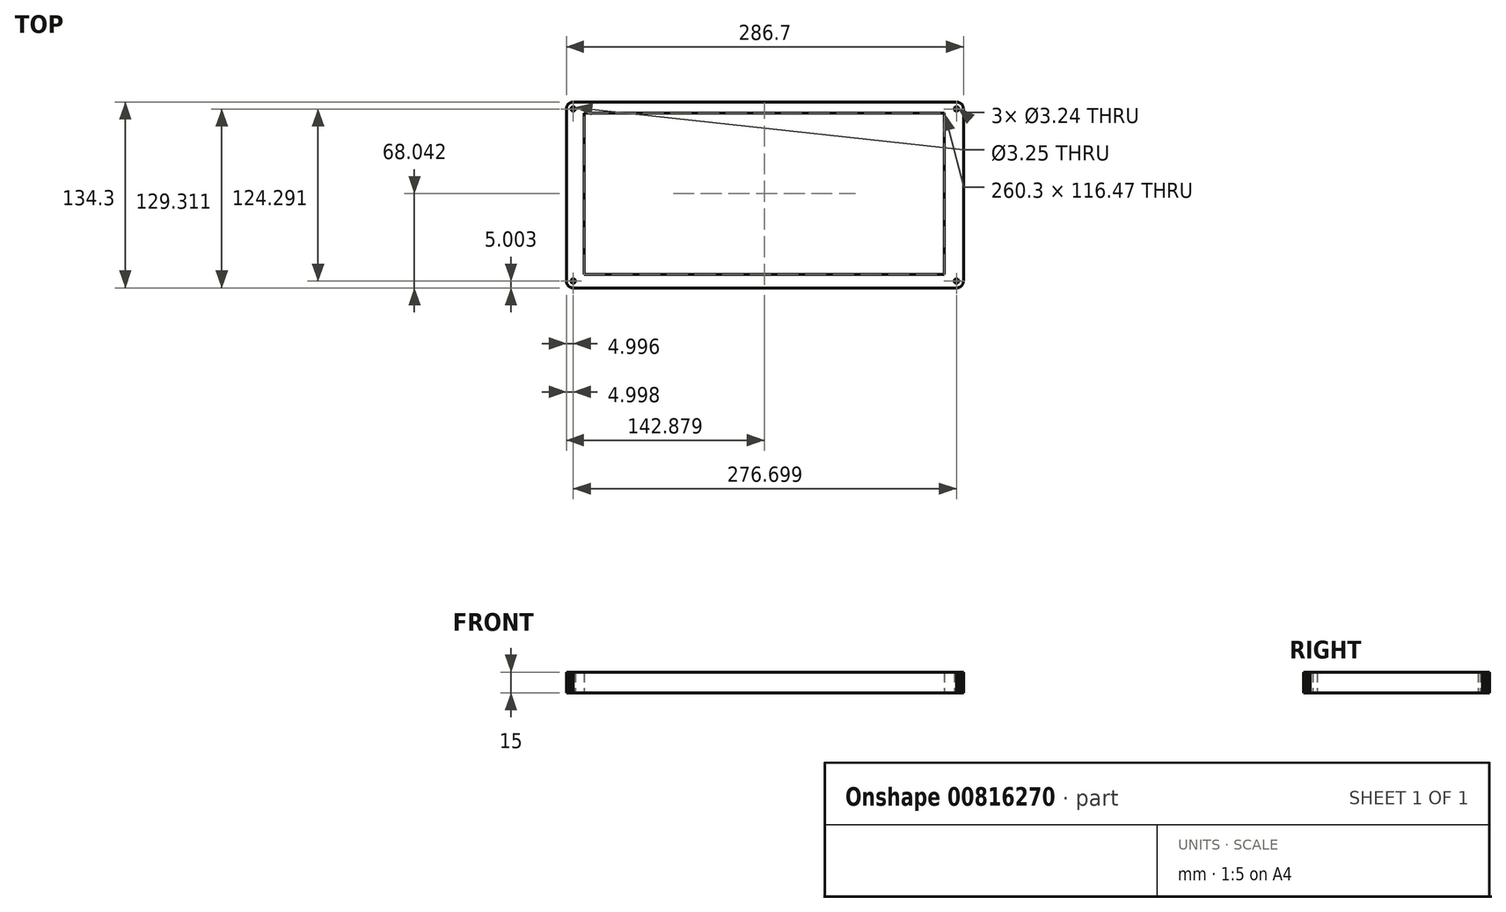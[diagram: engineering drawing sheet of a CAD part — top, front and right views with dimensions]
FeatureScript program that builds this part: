
annotation { "Feature Type Name" : "Feature", "Feature Type Description" : "" }
export const myFeature = defineFeature(function(context is Context, id is Id, definition is map)
    precondition{}
    {
        {
            var Q0;
            Q0=qCreatedBy(makeId("Top.planeOp"),FACE);
            var sketch = newSketch(context, id + "F0", { "sketchPlane" : qUnion([Q0])});
            skLineSegment(sketch, "E0", {"start": v(138.35, 67.15) * mm, "end": v(138.74, 67.13) * mm});
            skLineSegment(sketch, "E1", {"start": v(138.74, 67.13) * mm, "end": v(139.13, 67.09) * mm});
            skLineSegment(sketch, "E2", {"start": v(139.13, 67.09) * mm, "end": v(139.52, 67.01) * mm});
            skLineSegment(sketch, "E3", {"start": v(139.52, 67.01) * mm, "end": v(139.9, 66.9) * mm});
            skLineSegment(sketch, "E4", {"start": v(139.9, 66.9) * mm, "end": v(140.26, 66.77) * mm});
            skLineSegment(sketch, "E5", {"start": v(140.26, 66.77) * mm, "end": v(140.62, 66.6) * mm});
            skLineSegment(sketch, "E6", {"start": v(140.62, 66.6) * mm, "end": v(140.96, 66.41) * mm});
            skLineSegment(sketch, "E7", {"start": v(140.96, 66.41) * mm, "end": v(141.29, 66.2) * mm});
            skLineSegment(sketch, "E8", {"start": v(141.29, 66.2) * mm, "end": v(141.6, 65.95) * mm});
            skLineSegment(sketch, "E9", {"start": v(141.6, 65.95) * mm, "end": v(141.89, 65.69) * mm});
            skLineSegment(sketch, "E10", {"start": v(141.89, 65.69) * mm, "end": v(142.15, 65.4) * mm});
            skLineSegment(sketch, "E11", {"start": v(142.15, 65.4) * mm, "end": v(142.4, 65.09) * mm});
            skLineSegment(sketch, "E12", {"start": v(142.4, 65.09) * mm, "end": v(142.61, 64.76) * mm});
            skLineSegment(sketch, "E13", {"start": v(142.61, 64.76) * mm, "end": v(142.8, 64.42) * mm});
            skLineSegment(sketch, "E14", {"start": v(142.8, 64.42) * mm, "end": v(142.97, 64.06) * mm});
            skLineSegment(sketch, "E15", {"start": v(142.97, 64.06) * mm, "end": v(143.1, 63.7) * mm});
            skLineSegment(sketch, "E16", {"start": v(143.1, 63.7) * mm, "end": v(143.21, 63.32) * mm});
            skLineSegment(sketch, "E17", {"start": v(143.21, 63.32) * mm, "end": v(143.29, 62.93) * mm});
            skLineSegment(sketch, "E18", {"start": v(143.29, 62.93) * mm, "end": v(143.33, 62.54) * mm});
            skLineSegment(sketch, "E19", {"start": v(143.33, 62.54) * mm, "end": v(143.35, 62.15) * mm});
            skLineSegment(sketch, "E20", {"start": v(143.35, 62.15) * mm, "end": v(143.35, -62.15) * mm});
            skLineSegment(sketch, "E21", {"start": v(143.35, -62.15) * mm, "end": v(143.33, -62.54) * mm});
            skLineSegment(sketch, "E22", {"start": v(143.33, -62.54) * mm, "end": v(143.29, -62.93) * mm});
            skLineSegment(sketch, "E23", {"start": v(143.29, -62.93) * mm, "end": v(143.21, -63.32) * mm});
            skLineSegment(sketch, "E24", {"start": v(143.21, -63.32) * mm, "end": v(143.1, -63.7) * mm});
            skLineSegment(sketch, "E25", {"start": v(143.1, -63.7) * mm, "end": v(142.97, -64.06) * mm});
            skLineSegment(sketch, "E26", {"start": v(142.97, -64.06) * mm, "end": v(142.8, -64.42) * mm});
            skLineSegment(sketch, "E27", {"start": v(142.8, -64.42) * mm, "end": v(142.61, -64.76) * mm});
            skLineSegment(sketch, "E28", {"start": v(142.61, -64.76) * mm, "end": v(142.4, -65.09) * mm});
            skLineSegment(sketch, "E29", {"start": v(142.4, -65.09) * mm, "end": v(142.15, -65.4) * mm});
            skLineSegment(sketch, "E30", {"start": v(142.15, -65.4) * mm, "end": v(141.89, -65.69) * mm});
            skLineSegment(sketch, "E31", {"start": v(141.89, -65.69) * mm, "end": v(141.6, -65.95) * mm});
            skLineSegment(sketch, "E32", {"start": v(141.6, -65.95) * mm, "end": v(141.29, -66.2) * mm});
            skLineSegment(sketch, "E33", {"start": v(141.29, -66.2) * mm, "end": v(140.96, -66.41) * mm});
            skLineSegment(sketch, "E34", {"start": v(140.96, -66.41) * mm, "end": v(140.62, -66.6) * mm});
            skLineSegment(sketch, "E35", {"start": v(140.62, -66.6) * mm, "end": v(140.26, -66.77) * mm});
            skLineSegment(sketch, "E36", {"start": v(140.26, -66.77) * mm, "end": v(139.9, -66.9) * mm});
            skLineSegment(sketch, "E37", {"start": v(139.9, -66.9) * mm, "end": v(139.52, -67.01) * mm});
            skLineSegment(sketch, "E38", {"start": v(139.52, -67.01) * mm, "end": v(139.13, -67.09) * mm});
            skLineSegment(sketch, "E39", {"start": v(139.13, -67.09) * mm, "end": v(138.74, -67.13) * mm});
            skLineSegment(sketch, "E40", {"start": v(138.74, -67.13) * mm, "end": v(138.35, -67.15) * mm});
            skLineSegment(sketch, "E41", {"start": v(138.35, -67.15) * mm, "end": v(-138.35, -67.15) * mm});
            skLineSegment(sketch, "E42", {"start": v(-138.35, -67.15) * mm, "end": v(-138.74, -67.13) * mm});
            skLineSegment(sketch, "E43", {"start": v(-138.74, -67.13) * mm, "end": v(-139.13, -67.09) * mm});
            skLineSegment(sketch, "E44", {"start": v(-139.13, -67.09) * mm, "end": v(-139.52, -67.01) * mm});
            skLineSegment(sketch, "E45", {"start": v(-139.52, -67.01) * mm, "end": v(-139.9, -66.9) * mm});
            skLineSegment(sketch, "E46", {"start": v(-139.9, -66.9) * mm, "end": v(-140.26, -66.77) * mm});
            skLineSegment(sketch, "E47", {"start": v(-140.26, -66.77) * mm, "end": v(-140.62, -66.6) * mm});
            skLineSegment(sketch, "E48", {"start": v(-140.62, -66.6) * mm, "end": v(-140.96, -66.41) * mm});
            skLineSegment(sketch, "E49", {"start": v(-140.96, -66.41) * mm, "end": v(-141.29, -66.2) * mm});
            skLineSegment(sketch, "E50", {"start": v(-141.29, -66.2) * mm, "end": v(-141.6, -65.95) * mm});
            skLineSegment(sketch, "E51", {"start": v(-141.6, -65.95) * mm, "end": v(-141.89, -65.69) * mm});
            skLineSegment(sketch, "E52", {"start": v(-141.89, -65.69) * mm, "end": v(-142.15, -65.4) * mm});
            skLineSegment(sketch, "E53", {"start": v(-142.15, -65.4) * mm, "end": v(-142.4, -65.09) * mm});
            skLineSegment(sketch, "E54", {"start": v(-142.4, -65.09) * mm, "end": v(-142.61, -64.76) * mm});
            skLineSegment(sketch, "E55", {"start": v(-142.61, -64.76) * mm, "end": v(-142.8, -64.42) * mm});
            skLineSegment(sketch, "E56", {"start": v(-142.8, -64.42) * mm, "end": v(-142.97, -64.06) * mm});
            skLineSegment(sketch, "E57", {"start": v(-142.97, -64.06) * mm, "end": v(-143.1, -63.7) * mm});
            skLineSegment(sketch, "E58", {"start": v(-143.1, -63.7) * mm, "end": v(-143.21, -63.32) * mm});
            skLineSegment(sketch, "E59", {"start": v(-143.21, -63.32) * mm, "end": v(-143.29, -62.93) * mm});
            skLineSegment(sketch, "E60", {"start": v(-143.29, -62.93) * mm, "end": v(-143.33, -62.54) * mm});
            skLineSegment(sketch, "E61", {"start": v(-143.33, -62.54) * mm, "end": v(-143.35, -62.15) * mm});
            skLineSegment(sketch, "E62", {"start": v(-143.35, -62.15) * mm, "end": v(-143.35, 62.15) * mm});
            skLineSegment(sketch, "E63", {"start": v(-143.35, 62.15) * mm, "end": v(-143.33, 62.54) * mm});
            skLineSegment(sketch, "E64", {"start": v(-143.33, 62.54) * mm, "end": v(-143.29, 62.93) * mm});
            skLineSegment(sketch, "E65", {"start": v(-143.29, 62.93) * mm, "end": v(-143.21, 63.32) * mm});
            skLineSegment(sketch, "E66", {"start": v(-143.21, 63.32) * mm, "end": v(-143.1, 63.7) * mm});
            skLineSegment(sketch, "E67", {"start": v(-143.1, 63.7) * mm, "end": v(-142.97, 64.06) * mm});
            skLineSegment(sketch, "E68", {"start": v(-142.97, 64.06) * mm, "end": v(-142.8, 64.42) * mm});
            skLineSegment(sketch, "E69", {"start": v(-142.8, 64.42) * mm, "end": v(-142.61, 64.76) * mm});
            skLineSegment(sketch, "E70", {"start": v(-142.61, 64.76) * mm, "end": v(-142.4, 65.09) * mm});
            skLineSegment(sketch, "E71", {"start": v(-142.4, 65.09) * mm, "end": v(-142.15, 65.4) * mm});
            skLineSegment(sketch, "E72", {"start": v(-142.15, 65.4) * mm, "end": v(-141.89, 65.69) * mm});
            skLineSegment(sketch, "E73", {"start": v(-141.89, 65.69) * mm, "end": v(-141.6, 65.95) * mm});
            skLineSegment(sketch, "E74", {"start": v(-141.6, 65.95) * mm, "end": v(-141.29, 66.2) * mm});
            skLineSegment(sketch, "E75", {"start": v(-141.29, 66.2) * mm, "end": v(-140.96, 66.41) * mm});
            skLineSegment(sketch, "E76", {"start": v(-140.96, 66.41) * mm, "end": v(-140.62, 66.6) * mm});
            skLineSegment(sketch, "E77", {"start": v(-140.62, 66.6) * mm, "end": v(-140.26, 66.77) * mm});
            skLineSegment(sketch, "E78", {"start": v(-140.26, 66.77) * mm, "end": v(-139.9, 66.9) * mm});
            skLineSegment(sketch, "E79", {"start": v(-139.9, 66.9) * mm, "end": v(-139.52, 67.01) * mm});
            skLineSegment(sketch, "E80", {"start": v(-139.52, 67.01) * mm, "end": v(-139.13, 67.09) * mm});
            skLineSegment(sketch, "E81", {"start": v(-139.13, 67.09) * mm, "end": v(-138.74, 67.13) * mm});
            skLineSegment(sketch, "E82", {"start": v(-138.74, 67.13) * mm, "end": v(-138.35, 67.15) * mm});
            skLineSegment(sketch, "E83", {"start": v(-138.35, 67.15) * mm, "end": v(138.35, 67.15) * mm});
            skCircle(sketch, "E84", {"center": v(-138.35, -62.14) * mm, "radius": 1.62 * mm});
            skCircle(sketch, "E85", {"center": v(-138.35, 62.16) * mm, "radius": 1.62 * mm});
            skCircle(sketch, "E86", {"center": v(138.35, -62.15) * mm, "radius": 1.62 * mm});
            skCircle(sketch, "E87", {"center": v(138.34, 62.14) * mm, "radius": 1.62 * mm});
            skLineSegment(sketch, "E88.bottom", {"start": v(-130.62, -57.34) * mm, "end": v(129.68, -57.34) * mm});
            skLineSegment(sketch, "E88.top", {"start": v(-130.62, 59.13) * mm, "end": v(129.68, 59.13) * mm});
            skLineSegment(sketch, "E88.left", {"start": v(-130.62, -57.34) * mm, "end": v(-130.62, 59.13) * mm});
            skLineSegment(sketch, "E88.right", {"start": v(129.68, -57.34) * mm, "end": v(129.68, 59.13) * mm});
            skSolve(sketch);
        }
        {
            var Q0;
            Q0=makeQuery(id+"F0.imprint","IMPRINT",FACE,{"disambiguationData":[TD([[makeQuery(id+"F0.imprint","IMPRINT",EDGE,{"derivedFrom":sQuery(id+"F0.wireOp",EDGE,"E0")}),-1.0]])]});
            extrude(context, id + "F1", {"entities" : qUnion([Q0]), "depth" : 15 * mm, "offsetDistance" : 25.4 * mm});
        }
    });
